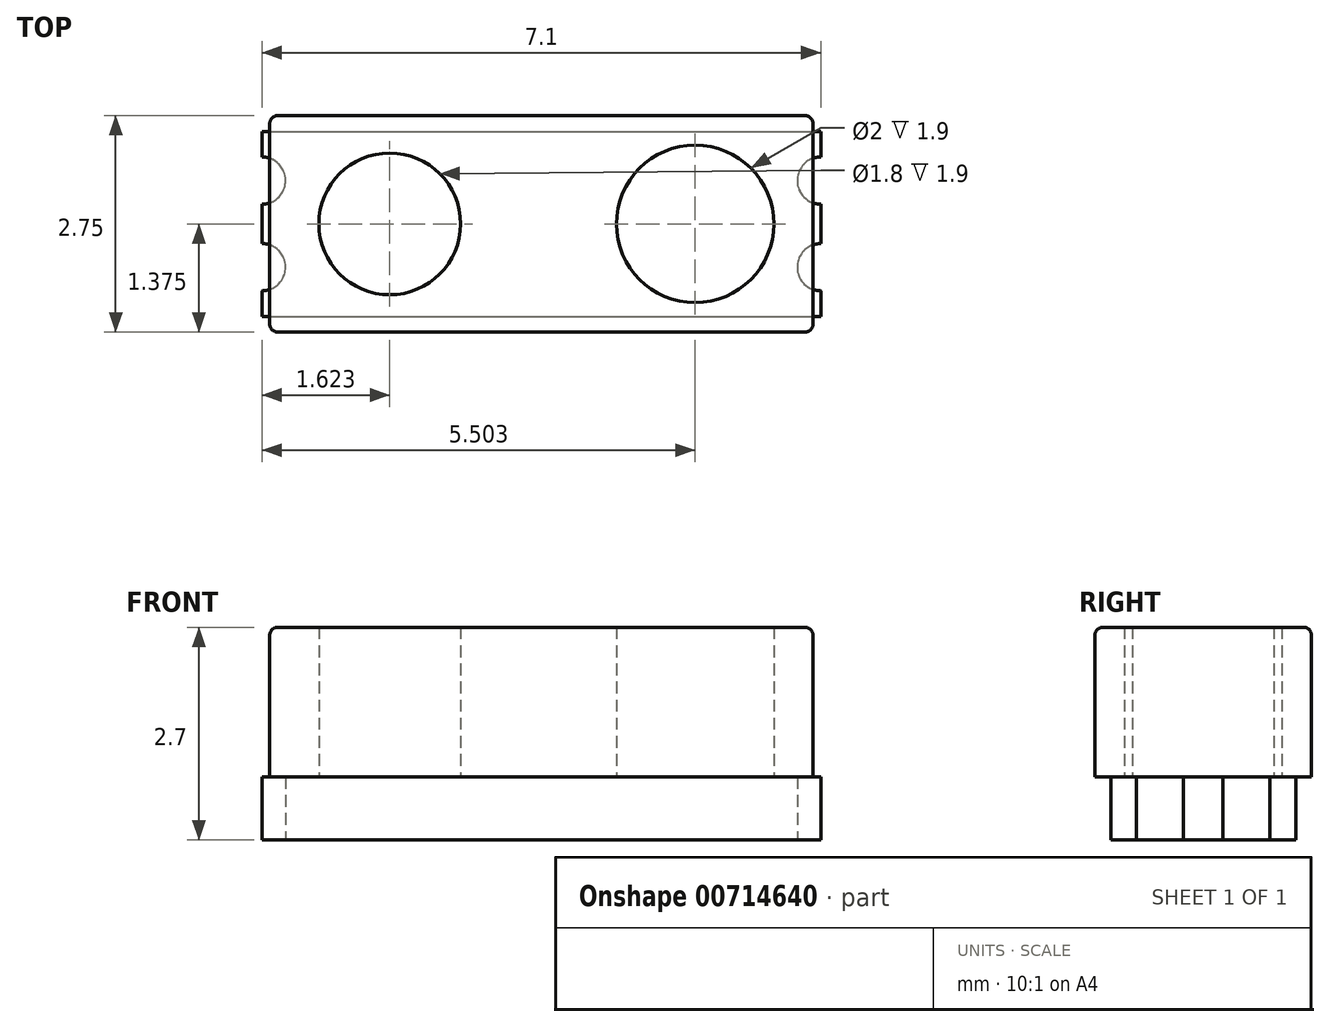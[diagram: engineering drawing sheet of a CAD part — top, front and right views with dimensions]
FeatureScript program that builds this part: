
annotation { "Feature Type Name" : "Feature", "Feature Type Description" : "" }
export const myFeature = defineFeature(function(context is Context, id is Id, definition is map)
    precondition{}
    {
        {
            var Q0;
            Q0=qCreatedBy(makeId("Top.planeOp"),FACE);
            var sketch = newSketch(context, id + "F0", { "sketchPlane" : qUnion([Q0])});
            skLineSegment(sketch, "E0.bottom", {"start": v(0, 0) * mm, "end": v(7.1, 0) * mm});
            skLineSegment(sketch, "E0.top", {"start": v(0, 2.35) * mm, "end": v(7.1, 2.35) * mm});
            skLineSegment(sketch, "E0.left", {"start": v(0, 0) * mm, "end": v(0, 2.35) * mm});
            skLineSegment(sketch, "E0.right", {"start": v(7.1, 0) * mm, "end": v(7.1, 2.35) * mm});
            skCircle(sketch, "E1", {"center": v(0, 0.63) * mm, "radius": 0.3 * mm});
            skCircle(sketch, "E2", {"center": v(0, 1.73) * mm, "radius": 0.3 * mm});
            skCircle(sketch, "E3", {"center": v(7.1, 1.73) * mm, "radius": 0.3 * mm});
            skCircle(sketch, "E4", {"center": v(7.1, 0.63) * mm, "radius": 0.3 * mm});
            skSolve(sketch);
        }
        {
            var Q0;
            Q0=makeQuery(id+"F0.imprint","IMPRINT",FACE,{"disambiguationData":[TD([[makeQuery(id+"F0.imprint","IMPRINT",EDGE,{"derivedFrom":sQuery(id+"F0.wireOp",EDGE,"E0.bottom")}),1.0]])]});
            extrude(context, id + "F1", {"entities" : qUnion([Q0]), "depth" : 0.8 * mm, "offsetDistance" : 25 * mm});
        }
        {
            var Q0;
            Q0=makeQuery(id+"F1.opExtrude","CAP_FACE",FACE,{"disambiguationData":[OSD([sQuery(id+"F0.wireOp",EDGE,"E0.bottom"),sQuery(id+"F0.wireOp",EDGE,"E0.top"),sQuery(id+"F0.wireOp",EDGE,"E0.left"),sQuery(id+"F0.wireOp",EDGE,"E0.right"),sQuery(id+"F0.wireOp",EDGE,"E1"),sQuery(id+"F0.wireOp",EDGE,"E2"),sQuery(id+"F0.wireOp",EDGE,"E3"),sQuery(id+"F0.wireOp",EDGE,"E4")])],"isStart":false});
            var sketch = newSketch(context, id + "F2", { "sketchPlane" : qUnion([Q0])});
            skLineSegment(sketch, "E5.bottom", {"start": v(0.1, 2.55) * mm, "end": v(7, 2.55) * mm});
            skLineSegment(sketch, "E5.top", {"start": v(0.1, -0.2) * mm, "end": v(7, -0.2) * mm});
            skLineSegment(sketch, "E5.left", {"start": v(0.1, 2.55) * mm, "end": v(0.1, -0.2) * mm});
            skLineSegment(sketch, "E5.right", {"start": v(7, 2.55) * mm, "end": v(7, -0.2) * mm});
            skCircle(sketch, "E6", {"center": v(1.62, 1.18) * mm, "radius": 0.9 * mm});
            skCircle(sketch, "E7", {"center": v(5.5, 1.18) * mm, "radius": 1 * mm});
            skSolve(sketch);
        }
        {
            var Q0;
            Q0=makeQuery(id+"F2.imprint","IMPRINT",FACE,{"disambiguationData":[TD([[makeQuery(id+"F2.imprint","IMPRINT",EDGE,{"derivedFrom":sQuery(id+"F2.wireOp",EDGE,"E6")}),-1.0]])]});
            var Q1;
            {var subQ0=sQuery(id+"F2.wireOp",EDGE,"E5.bottom");Q1=makeQuery(id+"F2.imprint","IMPRINT",FACE,{"disambiguationData":[TD([[makeQuery(id+"F2.imprint","IMPRINT",EDGE,{"derivedFrom":subQ0}),-1.0]])]});}
            var Q2;
            {var subQ0=sQuery(id+"F2.wireOp",EDGE,"E5.top");Q2=makeQuery(id+"F2.imprint","IMPRINT",FACE,{"disambiguationData":[TD([[makeQuery(id+"F2.imprint","IMPRINT",EDGE,{"derivedFrom":subQ0}),1.0]])]});}
            var Q3;
            {var subQ0=sQuery(id+"F2.wireOp",EDGE,"E5.left");var subQ1=makeQuery(id+"F1.opExtrude","CAP_EDGE",EDGE,{"disambiguationData":[OSD([sQuery(id+"F0.wireOp",EDGE,"E1")])],"isStart":false});var subQ2=makeQuery(id+"F2.imprint","INTERSECT",VERTEX,{"disambiguationData":[OD(0.0)],"derivedFrom":[subQ1,subQ0]});Q3=makeQuery(id+"F2.imprint","IMPRINT",FACE,{"disambiguationData":[TD([[makeQuery(id+"F2.imprint","IMPRINT",EDGE,{"disambiguationData":[TD([[subQ2,-1.0]])],"derivedFrom":subQ0}),1.0]])]});}
            var Q4;
            {var subQ0=sQuery(id+"F2.wireOp",EDGE,"E5.left");var subQ1=makeQuery(id+"F1.opExtrude","CAP_EDGE",EDGE,{"disambiguationData":[OSD([sQuery(id+"F0.wireOp",EDGE,"E2")])],"isStart":false});var subQ2=makeQuery(id+"F2.imprint","INTERSECT",VERTEX,{"disambiguationData":[OD(0.0)],"derivedFrom":[subQ1,subQ0]});Q4=makeQuery(id+"F2.imprint","IMPRINT",FACE,{"disambiguationData":[TD([[makeQuery(id+"F2.imprint","IMPRINT",EDGE,{"disambiguationData":[TD([[subQ2,-1.0]])],"derivedFrom":subQ0}),1.0]])]});}
            var Q5;
            {var subQ0=sQuery(id+"F2.wireOp",EDGE,"E5.right");var subQ1=makeQuery(id+"F1.opExtrude","CAP_EDGE",EDGE,{"disambiguationData":[OSD([sQuery(id+"F0.wireOp",EDGE,"E3")])],"isStart":false});var subQ2=makeQuery(id+"F2.imprint","INTERSECT",VERTEX,{"disambiguationData":[OD(0.0)],"derivedFrom":[subQ1,subQ0]});Q5=makeQuery(id+"F2.imprint","IMPRINT",FACE,{"disambiguationData":[TD([[makeQuery(id+"F2.imprint","IMPRINT",EDGE,{"disambiguationData":[TD([[subQ2,-1.0]])],"derivedFrom":subQ0}),-1.0]])]});}
            var Q6;
            {var subQ0=sQuery(id+"F2.wireOp",EDGE,"E5.right");var subQ1=makeQuery(id+"F1.opExtrude","CAP_EDGE",EDGE,{"disambiguationData":[OSD([sQuery(id+"F0.wireOp",EDGE,"E4")])],"isStart":false});var subQ2=makeQuery(id+"F2.imprint","INTERSECT",VERTEX,{"disambiguationData":[OD(0.0)],"derivedFrom":[subQ1,subQ0]});Q6=makeQuery(id+"F2.imprint","IMPRINT",FACE,{"disambiguationData":[TD([[makeQuery(id+"F2.imprint","IMPRINT",EDGE,{"disambiguationData":[TD([[subQ2,-1.0]])],"derivedFrom":subQ0}),-1.0]])]});}
            extrude(context, id + "F3", {"entities" : qUnion([Q0, Q1, Q2, Q3, Q4, Q5, Q6]), "operationType" : NewBodyOperationType.ADD, "depth" : 1.9 * mm, "offsetDistance" : 25 * mm});
        }
        {
            var Q0;
            Q0=makeQuery(id+"F3.opExtrude","CAP_EDGE",EDGE,{"disambiguationData":[OSD([sQuery(id+"F2.wireOp",EDGE,"E5.left")])],"isStart":false});
            var Q1;
            Q1=makeQuery(id+"F3.opExtrude","SWEPT_EDGE",EDGE,{"disambiguationData":[OSD([sQuery(id+"F2.wireOp",EDGE,"E5.top"),sQuery(id+"F2.wireOp",EDGE,"E5.left")])]});
            var Q2;
            Q2=makeQuery(id+"F3.opExtrude","SWEPT_EDGE",EDGE,{"disambiguationData":[OSD([sQuery(id+"F2.wireOp",EDGE,"E5.bottom"),sQuery(id+"F2.wireOp",EDGE,"E5.left")])]});
            var Q3;
            Q3=makeQuery(id+"F3.opExtrude","SWEPT_EDGE",EDGE,{"disambiguationData":[OSD([sQuery(id+"F2.wireOp",EDGE,"E5.top"),sQuery(id+"F2.wireOp",EDGE,"E5.right")])]});
            var Q4;
            Q4=makeQuery(id+"F3.opExtrude","SWEPT_EDGE",EDGE,{"disambiguationData":[OSD([sQuery(id+"F2.wireOp",EDGE,"E5.bottom"),sQuery(id+"F2.wireOp",EDGE,"E5.right")])]});
            var Q5;
            Q5=makeQuery(id+"F3.opExtrude","CAP_EDGE",EDGE,{"disambiguationData":[OSD([sQuery(id+"F2.wireOp",EDGE,"E5.bottom")])],"isStart":false});
            var Q6;
            Q6=makeQuery(id+"F3.opExtrude","CAP_EDGE",EDGE,{"disambiguationData":[OSD([sQuery(id+"F2.wireOp",EDGE,"E5.top")])],"isStart":false});
            var Q7;
            Q7=makeQuery(id+"F3.opExtrude","CAP_EDGE",EDGE,{"disambiguationData":[OSD([sQuery(id+"F2.wireOp",EDGE,"E5.right")])],"isStart":false});
            fillet(context, id + "F4", {"entities" : qUnion([Q0, Q1, Q2, Q3, Q4, Q5, Q6, Q7]), "radius" : 0.1 * mm, "tangentPropagation" : true, "allowEdgeOverflow" : false});
        }
    });
